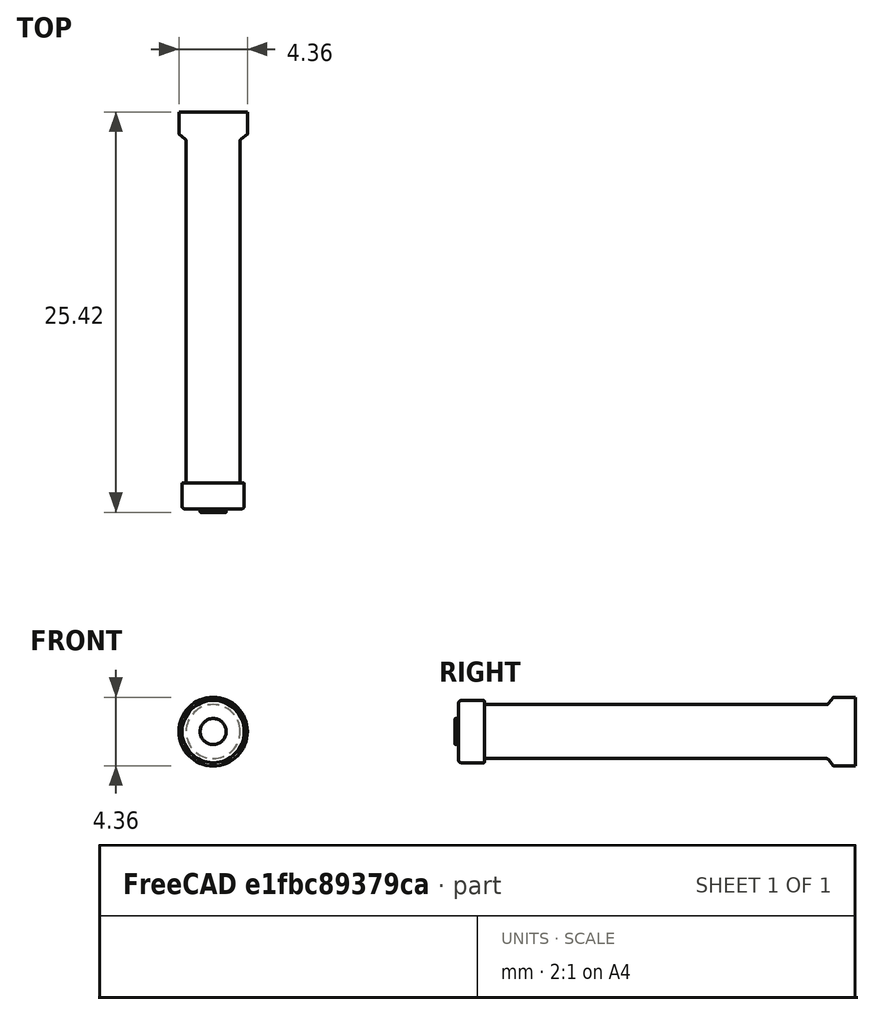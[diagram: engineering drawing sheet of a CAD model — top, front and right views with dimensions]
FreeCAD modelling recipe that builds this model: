
FCSTD DOCUMENT  (FreeCAD 0.20R29410 (Git))
Label: EX_Handle
License: All rights reserved
LicenseURL: http://en.wikipedia.org/wiki/All_rights_reserved
objects: Image::ImagePlane×1, Sketcher::SketchObject×1, PartDesign::Revolution×1, PartDesign::Body×1
note: 4 computed .brp shape members not serialized (recipe doc carries the construction recipe); baked Part::Feature solids carry a one-line shape summary decoded from their .brp

FEATURE [Image::ImagePlane] ImagePlane
  Placement = pos=(17.5725,0,0) rot=(0,0,1;0rad)
  XSize = 123.545
  YSize = 150.529
FEATURE [Sketcher::SketchObject] Sketch
  FullyConstrained = false
  sketch-geometry (17):
    g0: LineSegment StartX=-2.18014 StartY=-47.1294 StartZ=0 EndX=-2.18014 EndY=-48.5065 EndZ=0
    g1: LineSegment StartX=-2.16845 StartY=-48.5305 StartZ=0 EndX=-1.77948 EndY=-48.8363 EndZ=0
    g2: LineSegment StartX=-1.71556 StartY=-48.9678 StartZ=0 EndX=-1.71556 EndY=-70.6247 EndZ=0
    g3: LineSegment StartX=-1.78543 StartY=-70.6945 StartZ=0 EndX=-1.93517 EndY=-70.6945 EndZ=0
    g4: LineSegment StartX=-1.97547 StartY=-70.7348 StartZ=0 EndX=-1.97547 EndY=-72.1702 EndZ=0
    g5: LineSegment StartX=-1.81812 StartY=-72.3278 StartZ=0 EndX=-0.86072 EndY=-72.3296 EndZ=0
    g6: LineSegment StartX=-0.829025 StartY=-72.3613 StartZ=0 EndX=-0.829025 EndY=-72.5238 EndZ=0
    g7: LineSegment StartX=-0.802578 StartY=-72.5503 StartZ=0 EndX=0 EndY=-72.5503 EndZ=0
    g8: ArcOfCircle CenterX=-2.14953 CenterY=-48.5065 CenterZ=0 NormalX=0 NormalY=0 NormalZ=1 AngleXU=0 Radius=0.0306164 StartAngle=3.14159 EndAngle=4.04623
    g9: ArcOfCircle CenterX=-1.88288 CenterY=-48.9678 CenterZ=0 NormalX=0 NormalY=0 NormalZ=1 AngleXU=0 Radius=0.167316 StartAngle=-5.3e-15 EndAngle=0.904641
    g10: ArcOfCircle CenterX=-1.78543 CenterY=-70.6247 CenterZ=0 NormalX=0 NormalY=0 NormalZ=1 AngleXU=0 Radius=0.0698678 StartAngle=4.71239 EndAngle=6.28319
    g11: ArcOfCircle CenterX=-1.93517 CenterY=-70.7348 CenterZ=0 NormalX=0 NormalY=0 NormalZ=1 AngleXU=0 Radius=0.0402957 StartAngle=1.5708 EndAngle=3.14159
    g12: ArcOfCircle CenterX=-1.81783 CenterY=-72.1702 CenterZ=0 NormalX=0 NormalY=0 NormalZ=1 AngleXU=0 Radius=0.157637 StartAngle=3.14159 EndAngle=4.71054
    g13: ArcOfCircle CenterX=-0.860778 CenterY=-72.3613 CenterZ=0 NormalX=0 NormalY=0 NormalZ=1 AngleXU=0 Radius=0.031753 StartAngle=-6.2e-15 EndAngle=1.56895
    g14: ArcOfCircle CenterX=-0.802578 CenterY=-72.5238 CenterZ=0 NormalX=0 NormalY=0 NormalZ=1 AngleXU=0 Radius=0.026447 StartAngle=3.14159 EndAngle=4.71239
    g15: LineSegment StartX=0 StartY=-72.5503 StartZ=0 EndX=0 EndY=-47.1294 EndZ=0
    g16: LineSegment StartX=-2.18014 StartY=-47.1294 StartZ=0 EndX=0 EndY=-47.1294 EndZ=0
  constraints (26):
    c: Vertical(g0)
    c: Vertical(g2)
    c: Vertical(g4)
    c: Vertical(g6)
    c: PointOnObject(g7,g-2)
    c: Horizontal(g7)
    c: Horizontal(g3)
    c: Tangent(g0,g8) = -1.5708
    c: Tangent(g1,g8) = -1.5708
    c: Tangent(g1,g9) = 1.5708
    c: Tangent(g2,g9) = 1.5708
    c: Tangent(g2,g10) = 1.5708
    c: Tangent(g3,g10) = 1.5708
    c: Tangent(g3,g11) = -1.5708
    c: Tangent(g4,g11) = -1.5708
    c: Tangent(g4,g12) = -1.5708
    c: Tangent(g5,g12) = -1.5708
    c: Tangent(g5,g13) = 1.5708
    c: Tangent(g6,g13) = 1.5708
    c: Tangent(g6,g14) = -1.5708
    c: Tangent(g7,g14) = -1.5708
    c: PointOnObject(g15,g-2)
    c: Coincident(g16,g0)
    c: Coincident(g16,g15)
    c: Horizontal(g16)
    c: Coincident(g7,g15)
FEATURE [PartDesign::Revolution] Revolution
  Angle = 360
  Axis = (0,1,0)
  Base = (0,0,0)
  Profile = -> Sketch
  ReferenceAxis = -> Sketch [V_Axis]
FEATURE [PartDesign::Body] Body
  Group = -> [Sketch,Revolution]
  Origin = -> Origin
  Tip = -> Revolution
